# Revit family: Legrand XL³-S 630 16 módulos a la fila
name_source: partatom
category: Equipement électrique
units: mm (PartAtom-declared; Revit-internal decimal feet)

## family parameters
Basée sur le plan de construction = Non
Configuration du panneau = Deux colonnes, circuits au sein
Cote de connecteur circulaire = Utiliser le diamètre
Couper avec des vides une fois chargée = Non
Numéro OmniClass = 23.80.30.11.17
Partagée = Non
Point de calcul de pièce = Non
Titre OmniClass = Distribution Boards and Control Panels
Toujours verticalement = Oui
Type d'élément = Tableau de raccordement

## types (11) — shared parameters
Altura Básica = 100 mm  [stored 0.328084 ft]
Condiciones Generales de Uso = https://export.legrand.com
ETIM Class 6.0 = EC000261
Fabricant = Legrand
IK = 08
IP = 40
Image du type = XL3S_630_16M_337581_p_230129.jpg
Materia = Acero
RAL = 9003
URL = www.legrand.fr
anchura = 454 mm  [stored 1.4895 ft]
anchura asentamiento = 952 mm  [stored 3.12336 ft]
base = Oui
distancia antes de asentamiento = 454 mm  [stored 1.4895 ft]
distancia lado asentamiento = 249 mm  [stored 0.816929 ft]
kit acabado = Non
kit acabado 337960_337972 = Non
kit acabado 337961_337972 = Non
kit acabado 337962_337972 = Non
kit acabado 337963_337972 = Non
kit acabado 337964_337972 = Non
kit acabado 337965_337972 = Non
kit acabado 337966_337972 = Non
kit acabado 337967_337972 = Non
kit acabado 337968_337972 = Non
kit acabado 337969_337972 = Non
kit acabado 337970_337972 = Non
panele lateral derecho = Oui
panele lateral izquierdo = Oui
profundidad = 249 mm  [stored 0.816929 ft]
profundidad asentamiento = 703 mm  [stored 2.30643 ft]
puerta = Oui
zero-valued in all types: Elévation par défaut

## per-type parameters (varying)
- Envolvente de distribución - XL³ S 630 -  Metal - altura 750 - 16 módulos: Altura=924 mm  [stored 3.0315 ft]; Description=337521  Envolvente de distribución - XL³ S 630 -  Metal - altura 750 - 16 módulos; envoltura 337521=Oui; envoltura 337531=Non; envoltura 337541=Non; envoltura 337551=Non; envoltura 337561=Non; envoltura 337571=Non; envoltura 337581=Non; envoltura 337591=Non; envoltura 337601=Non; envoltura 337611=Non; envoltura 337621=Non; panele lateral derecho 337862=Oui; panele lateral derecho 337863=Non; panele lateral derecho 337864=Non; panele lateral derecho 337865=Non; panele lateral derecho 337866=Non; panele lateral derecho 337867=Non; panele lateral derecho 337868=Non; panele lateral derecho 337869=Non; panele lateral derecho 337870=Non; panele lateral derecho 337871=Non; panele lateral derecho 337872=Non; panele lateral izquierdo  337872=Non; panele lateral izquierdo 337862=Oui; panele lateral izquierdo 337863=Non; panele lateral izquierdo 337864=Non; panele lateral izquierdo 337865=Non; panele lateral izquierdo 337866=Non; panele lateral izquierdo 337867=Non; panele lateral izquierdo 337868=Non; panele lateral izquierdo 337869=Non; panele lateral izquierdo 337870=Non; panele lateral izquierdo 337871=Non; puerta 337641=Oui; puerta 337651=Non; puerta 337661=Non; puerta 337671=Non; puerta 337681=Non; puerta 337691=Non; puerta 337701=Non; puerta 337711=Non; puerta 337721=Non; puerta 337731=Non; puerta 337741=Non
- Envolvente de distribución - XL³ S 630 -  Metal - altura 900 - 16 módulos: Altura=1074 mm  [stored 3.52362 ft]; Description=337531  Envolvente de distribución - XL³ S 630 -  Metal - altura 900 - 16 módulos; envoltura 337521=Non; envoltura 337531=Oui; envoltura 337541=Non; envoltura 337551=Non; envoltura 337561=Non; envoltura 337571=Non; envoltura 337581=Non; envoltura 337591=Non; envoltura 337601=Non; envoltura 337611=Non; envoltura 337621=Non; panele lateral derecho 337862=Non; panele lateral derecho 337863=Oui; panele lateral derecho 337864=Non; panele lateral derecho 337865=Non; panele lateral derecho 337866=Non; panele lateral derecho 337867=Non; panele lateral derecho 337868=Non; panele lateral derecho 337869=Non; panele lateral derecho 337870=Non; panele lateral derecho 337871=Non; panele lateral derecho 337872=Non; panele lateral izquierdo  337872=Non; panele lateral izquierdo 337862=Non; panele lateral izquierdo 337863=Oui; panele lateral izquierdo 337864=Non; panele lateral izquierdo 337865=Non; panele lateral izquierdo 337866=Non; panele lateral izquierdo 337867=Non; panele lateral izquierdo 337868=Non; panele lateral izquierdo 337869=Non; panele lateral izquierdo 337870=Non; panele lateral izquierdo 337871=Non; puerta 337641=Non; puerta 337651=Oui; puerta 337661=Non; puerta 337671=Non; puerta 337681=Non; puerta 337691=Non; puerta 337701=Non; puerta 337711=Non; puerta 337721=Non; puerta 337731=Non; puerta 337741=Non
- Envolvente de distribución - XL³ S 630 -  Metal - altura 1050 - 16 módulos: Altura=1224 mm  [stored 4.01575 ft]; Description=337541  Envolvente de distribución - XL³ S 630 -  Metal - altura 1050 - 16 módulos; envoltura 337521=Non; envoltura 337531=Non; envoltura 337541=Oui; envoltura 337551=Non; envoltura 337561=Non; envoltura 337571=Non; envoltura 337581=Non; envoltura 337591=Non; envoltura 337601=Non; envoltura 337611=Non; envoltura 337621=Non; panele lateral derecho 337862=Non; panele lateral derecho 337863=Non; panele lateral derecho 337864=Oui; panele lateral derecho 337865=Non; panele lateral derecho 337866=Non; panele lateral derecho 337867=Non; panele lateral derecho 337868=Non; panele lateral derecho 337869=Non; panele lateral derecho 337870=Non; panele lateral derecho 337871=Non; panele lateral derecho 337872=Non; panele lateral izquierdo  337872=Non; panele lateral izquierdo 337862=Non; panele lateral izquierdo 337863=Non; panele lateral izquierdo 337864=Oui; panele lateral izquierdo 337865=Non; panele lateral izquierdo 337866=Non; panele lateral izquierdo 337867=Non; panele lateral izquierdo 337868=Non; panele lateral izquierdo 337869=Non; panele lateral izquierdo 337870=Non; panele lateral izquierdo 337871=Non; puerta 337641=Non; puerta 337651=Non; puerta 337661=Oui; puerta 337671=Non; puerta 337681=Non; puerta 337691=Non; puerta 337701=Non; puerta 337711=Non; puerta 337721=Non; puerta 337731=Non; puerta 337741=Non
- Envolvente de distribución - XL³ S 630 -  Metal - altura 1200 - 16 módulos: Altura=1374 mm  [stored 4.50787 ft]; Description=337551  Envolvente de distribución - XL³ S 630 -  Metal - altura 1200 - 16 módulos; envoltura 337521=Non; envoltura 337531=Non; envoltura 337541=Non; envoltura 337551=Oui; envoltura 337561=Non; envoltura 337571=Non; envoltura 337581=Non; envoltura 337591=Non; envoltura 337601=Non; envoltura 337611=Non; envoltura 337621=Non; panele lateral derecho 337862=Non; panele lateral derecho 337863=Non; panele lateral derecho 337864=Non; panele lateral derecho 337865=Oui; panele lateral derecho 337866=Non; panele lateral derecho 337867=Non; panele lateral derecho 337868=Non; panele lateral derecho 337869=Non; panele lateral derecho 337870=Non; panele lateral derecho 337871=Non; panele lateral derecho 337872=Non; panele lateral izquierdo  337872=Non; panele lateral izquierdo 337862=Non; panele lateral izquierdo 337863=Non; panele lateral izquierdo 337864=Non; panele lateral izquierdo 337865=Oui; panele lateral izquierdo 337866=Non; panele lateral izquierdo 337867=Non; panele lateral izquierdo 337868=Non; panele lateral izquierdo 337869=Non; panele lateral izquierdo 337870=Non; panele lateral izquierdo 337871=Non; puerta 337641=Non; puerta 337651=Non; puerta 337661=Non; puerta 337671=Oui; puerta 337681=Non; puerta 337691=Non; puerta 337701=Non; puerta 337711=Non; puerta 337721=Non; puerta 337731=Non; puerta 337741=Non
- Envolvente de distribución - XL³ S 630 -  Metal - altura 1350 - 16 módulos: Altura=1524 mm  [stored 5 ft]; Description=337561  Envolvente de distribución - XL³ S 630 -  Metal - altura 1350 - 16 módulos; envoltura 337521=Non; envoltura 337531=Non; envoltura 337541=Non; envoltura 337551=Non; envoltura 337561=Oui; envoltura 337571=Non; envoltura 337581=Non; envoltura 337591=Non; envoltura 337601=Non; envoltura 337611=Non; envoltura 337621=Non; panele lateral derecho 337862=Non; panele lateral derecho 337863=Non; panele lateral derecho 337864=Non; panele lateral derecho 337865=Non; panele lateral derecho 337866=Oui; panele lateral derecho 337867=Non; panele lateral derecho 337868=Non; panele lateral derecho 337869=Non; panele lateral derecho 337870=Non; panele lateral derecho 337871=Non; panele lateral derecho 337872=Non; panele lateral izquierdo  337872=Non; panele lateral izquierdo 337862=Non; panele lateral izquierdo 337863=Non; panele lateral izquierdo 337864=Non; panele lateral izquierdo 337865=Non; panele lateral izquierdo 337866=Oui; panele lateral izquierdo 337867=Non; panele lateral izquierdo 337868=Non; panele lateral izquierdo 337869=Non; panele lateral izquierdo 337870=Non; panele lateral izquierdo 337871=Non; puerta 337641=Non; puerta 337651=Non; puerta 337661=Non; puerta 337671=Non; puerta 337681=Oui; puerta 337691=Non; puerta 337701=Non; puerta 337711=Non; puerta 337721=Non; puerta 337731=Non; puerta 337741=Non
- Envolvente de distribución - XL³ S 630 -  Metal - altura 1500 - 16 módulos: Altura=1674 mm  [stored 5.49213 ft]; Description=337571  Envolvente de distribución - XL³ S 630 -  Metal - altura 1500 - 16 módulos; envoltura 337521=Non; envoltura 337531=Non; envoltura 337541=Non; envoltura 337551=Non; envoltura 337561=Non; envoltura 337571=Oui; envoltura 337581=Non; envoltura 337591=Non; envoltura 337601=Non; envoltura 337611=Non; envoltura 337621=Non; panele lateral derecho 337862=Non; panele lateral derecho 337863=Non; panele lateral derecho 337864=Non; panele lateral derecho 337865=Non; panele lateral derecho 337866=Non; panele lateral derecho 337867=Oui; panele lateral derecho 337868=Non; panele lateral derecho 337869=Non; panele lateral derecho 337870=Non; panele lateral derecho 337871=Non; panele lateral derecho 337872=Non; panele lateral izquierdo  337872=Non; panele lateral izquierdo 337862=Non; panele lateral izquierdo 337863=Non; panele lateral izquierdo 337864=Non; panele lateral izquierdo 337865=Non; panele lateral izquierdo 337866=Non; panele lateral izquierdo 337867=Oui; panele lateral izquierdo 337868=Non; panele lateral izquierdo 337869=Non; panele lateral izquierdo 337870=Non; panele lateral izquierdo 337871=Non; puerta 337641=Non; puerta 337651=Non; puerta 337661=Non; puerta 337671=Non; puerta 337681=Non; puerta 337691=Oui; puerta 337701=Non; puerta 337711=Non; puerta 337721=Non; puerta 337731=Non; puerta 337741=Non
- Envolvente de distribución - XL³ S 630 -  Metal - altura 1650 - 16 módulos: Altura=1824 mm  [stored 5.98425 ft]; Description=337581  Envolvente de distribución - XL³ S 630 -  Metal - altura 1650 - 16 módulos; envoltura 337521=Non; envoltura 337531=Non; envoltura 337541=Non; envoltura 337551=Non; envoltura 337561=Non; envoltura 337571=Non; envoltura 337581=Oui; envoltura 337591=Non; envoltura 337601=Non; envoltura 337611=Non; envoltura 337621=Non; panele lateral derecho 337862=Non; panele lateral derecho 337863=Non; panele lateral derecho 337864=Non; panele lateral derecho 337865=Non; panele lateral derecho 337866=Non; panele lateral derecho 337867=Non; panele lateral derecho 337868=Oui; panele lateral derecho 337869=Non; panele lateral derecho 337870=Non; panele lateral derecho 337871=Non; panele lateral derecho 337872=Non; panele lateral izquierdo  337872=Non; panele lateral izquierdo 337862=Non; panele lateral izquierdo 337863=Non; panele lateral izquierdo 337864=Non; panele lateral izquierdo 337865=Non; panele lateral izquierdo 337866=Non; panele lateral izquierdo 337867=Non; panele lateral izquierdo 337868=Oui; panele lateral izquierdo 337869=Non; panele lateral izquierdo 337870=Non; panele lateral izquierdo 337871=Non; puerta 337641=Non; puerta 337651=Non; puerta 337661=Non; puerta 337671=Non; puerta 337681=Non; puerta 337691=Non; puerta 337701=Oui; puerta 337711=Non; puerta 337721=Non; puerta 337731=Non; puerta 337741=Non
- Envolvente de distribución - XL³ S 630 -  Metal - altura 1800 - 16 módulos: Altura=1974 mm  [stored 6.47638 ft]; Description=337591  Envolvente de distribución - XL³ S 630 -  Metal - altura 1800 - 16 módulos; envoltura 337521=Non; envoltura 337531=Non; envoltura 337541=Non; envoltura 337551=Non; envoltura 337561=Non; envoltura 337571=Non; envoltura 337581=Non; envoltura 337591=Oui; envoltura 337601=Non; envoltura 337611=Non; envoltura 337621=Non; panele lateral derecho 337862=Non; panele lateral derecho 337863=Non; panele lateral derecho 337864=Non; panele lateral derecho 337865=Non; panele lateral derecho 337866=Non; panele lateral derecho 337867=Non; panele lateral derecho 337868=Non; panele lateral derecho 337869=Oui; panele lateral derecho 337870=Non; panele lateral derecho 337871=Non; panele lateral derecho 337872=Non; panele lateral izquierdo  337872=Non; panele lateral izquierdo 337862=Non; panele lateral izquierdo 337863=Non; panele lateral izquierdo 337864=Non; panele lateral izquierdo 337865=Non; panele lateral izquierdo 337866=Non; panele lateral izquierdo 337867=Non; panele lateral izquierdo 337868=Non; panele lateral izquierdo 337869=Oui; panele lateral izquierdo 337870=Non; panele lateral izquierdo 337871=Non; puerta 337641=Non; puerta 337651=Non; puerta 337661=Non; puerta 337671=Non; puerta 337681=Non; puerta 337691=Non; puerta 337701=Non; puerta 337711=Oui; puerta 337721=Non; puerta 337731=Non; puerta 337741=Non
- Envolvente de distribución - XL³ S 630 -  Metal - altura 1950 - 16 módulos: Altura=2124 mm  [stored 6.9685 ft]; Description=337601  Envolvente de distribución - XL³ S 630 -  Metal - altura 1950 - 16 módulos; envoltura 337521=Non; envoltura 337531=Non; envoltura 337541=Non; envoltura 337551=Non; envoltura 337561=Non; envoltura 337571=Non; envoltura 337581=Non; envoltura 337591=Non; envoltura 337601=Oui; envoltura 337611=Non; envoltura 337621=Non; panele lateral derecho 337862=Non; panele lateral derecho 337863=Non; panele lateral derecho 337864=Non; panele lateral derecho 337865=Non; panele lateral derecho 337866=Non; panele lateral derecho 337867=Non; panele lateral derecho 337868=Non; panele lateral derecho 337869=Non; panele lateral derecho 337870=Oui; panele lateral derecho 337871=Non; panele lateral derecho 337872=Non; panele lateral izquierdo  337872=Non; panele lateral izquierdo 337862=Non; panele lateral izquierdo 337863=Non; panele lateral izquierdo 337864=Non; panele lateral izquierdo 337865=Non; panele lateral izquierdo 337866=Non; panele lateral izquierdo 337867=Non; panele lateral izquierdo 337868=Non; panele lateral izquierdo 337869=Non; panele lateral izquierdo 337870=Oui; panele lateral izquierdo 337871=Non; puerta 337641=Non; puerta 337651=Non; puerta 337661=Non; puerta 337671=Non; puerta 337681=Non; puerta 337691=Non; puerta 337701=Non; puerta 337711=Non; puerta 337721=Oui; puerta 337731=Non; puerta 337741=Non
- Envolvente de distribución - XL³ S 630 -  Metal - altura 2100 - 16 módulos: Altura=2274 mm  [stored 7.46063 ft]; Description=337611  Envolvente de distribución - XL³ S 630 -  Metal - altura 2100 - 16 módulos; envoltura 337521=Non; envoltura 337531=Non; envoltura 337541=Non; envoltura 337551=Non; envoltura 337561=Non; envoltura 337571=Non; envoltura 337581=Non; envoltura 337591=Non; envoltura 337601=Non; envoltura 337611=Oui; envoltura 337621=Non; panele lateral derecho 337862=Non; panele lateral derecho 337863=Non; panele lateral derecho 337864=Non; panele lateral derecho 337865=Non; panele lateral derecho 337866=Non; panele lateral derecho 337867=Non; panele lateral derecho 337868=Non; panele lateral derecho 337869=Non; panele lateral derecho 337870=Non; panele lateral derecho 337871=Oui; panele lateral derecho 337872=Non; panele lateral izquierdo  337872=Non; panele lateral izquierdo 337862=Non; panele lateral izquierdo 337863=Non; panele lateral izquierdo 337864=Non; panele lateral izquierdo 337865=Non; panele lateral izquierdo 337866=Non; panele lateral izquierdo 337867=Non; panele lateral izquierdo 337868=Non; panele lateral izquierdo 337869=Non; panele lateral izquierdo 337870=Non; panele lateral izquierdo 337871=Oui; puerta 337641=Non; puerta 337651=Non; puerta 337661=Non; puerta 337671=Non; puerta 337681=Non; puerta 337691=Non; puerta 337701=Non; puerta 337711=Non; puerta 337721=Non; puerta 337731=Oui; puerta 337741=Non
- Envolvente de distribución - XL³ S 630 -  Metal - altura 2250 - 16 módulos: Altura=2424 mm  [stored 7.95276 ft]; Description=337621  Envolvente de distribución - XL³ S 630 -  Metal - altura 2250 - 16 módulos; envoltura 337521=Non; envoltura 337531=Non; envoltura 337541=Non; envoltura 337551=Non; envoltura 337561=Non; envoltura 337571=Non; envoltura 337581=Non; envoltura 337591=Non; envoltura 337601=Non; envoltura 337611=Non; envoltura 337621=Oui; panele lateral derecho 337862=Non; panele lateral derecho 337863=Non; panele lateral derecho 337864=Non; panele lateral derecho 337865=Non; panele lateral derecho 337866=Non; panele lateral derecho 337867=Non; panele lateral derecho 337868=Non; panele lateral derecho 337869=Non; panele lateral derecho 337870=Non; panele lateral derecho 337871=Non; panele lateral derecho 337872=Oui; panele lateral izquierdo  337872=Oui; panele lateral izquierdo 337862=Non; panele lateral izquierdo 337863=Non; panele lateral izquierdo 337864=Non; panele lateral izquierdo 337865=Non; panele lateral izquierdo 337866=Non; panele lateral izquierdo 337867=Non; panele lateral izquierdo 337868=Non; panele lateral izquierdo 337869=Non; panele lateral izquierdo 337870=Non; panele lateral izquierdo 337871=Non; puerta 337641=Non; puerta 337651=Non; puerta 337661=Non; puerta 337671=Non; puerta 337681=Non; puerta 337691=Non; puerta 337701=Non; puerta 337711=Non; puerta 337721=Non; puerta 337731=Non; puerta 337741=Oui

note: [stored X ft] marks values corroborated as IEEE doubles in the binary element streams (Revit-internal decimal feet)
